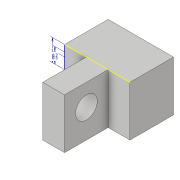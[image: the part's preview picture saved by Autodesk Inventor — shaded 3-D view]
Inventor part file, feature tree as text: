
AUTODESK INVENTOR PART (.ipt)
format: ipt  version: 2019 (Build 230136000, 136)  size: 112,128 bytes
history: native  units: mm
features: sketch x7, extrude x3
ambient origin geometry x8: Origin, YZ Plane, XZ Plane, XY Plane, X Axis, Y Axis, Z Axis, Center Point
bodies: Solid1 (feature_tree)
feature tree (10):
  extrude  "Extrusion1"  Depth=23.0mm
  sketch  "Sketch2"  dims[d2=20.0mm d3=0.0mm d4=10.0mm]
  sketch  "Sketch3"  dims[d5=7.0mm d6=5.0mm]
  sketch  "Sketch4"  dims[d7=10.0mm]
  sketch  "Sketch5"  dims[d8=10.0mm]
  extrude  "Extrusion2"  Depth=10.0mm
  extrude  "Extrusion3"  Depth=5.0mm
  sketch  "Sketch1"  dims[d0=30.0mm d1=23.0mm]
  sketch  "Sketch6"  dims[d9=20.0mm d10=0.0mm]
  sketch  "Sketch7"  dims[d11=10.0mm d12=10.0mm d13=10.0mm d14=20.0mm d15=0.0mm]
